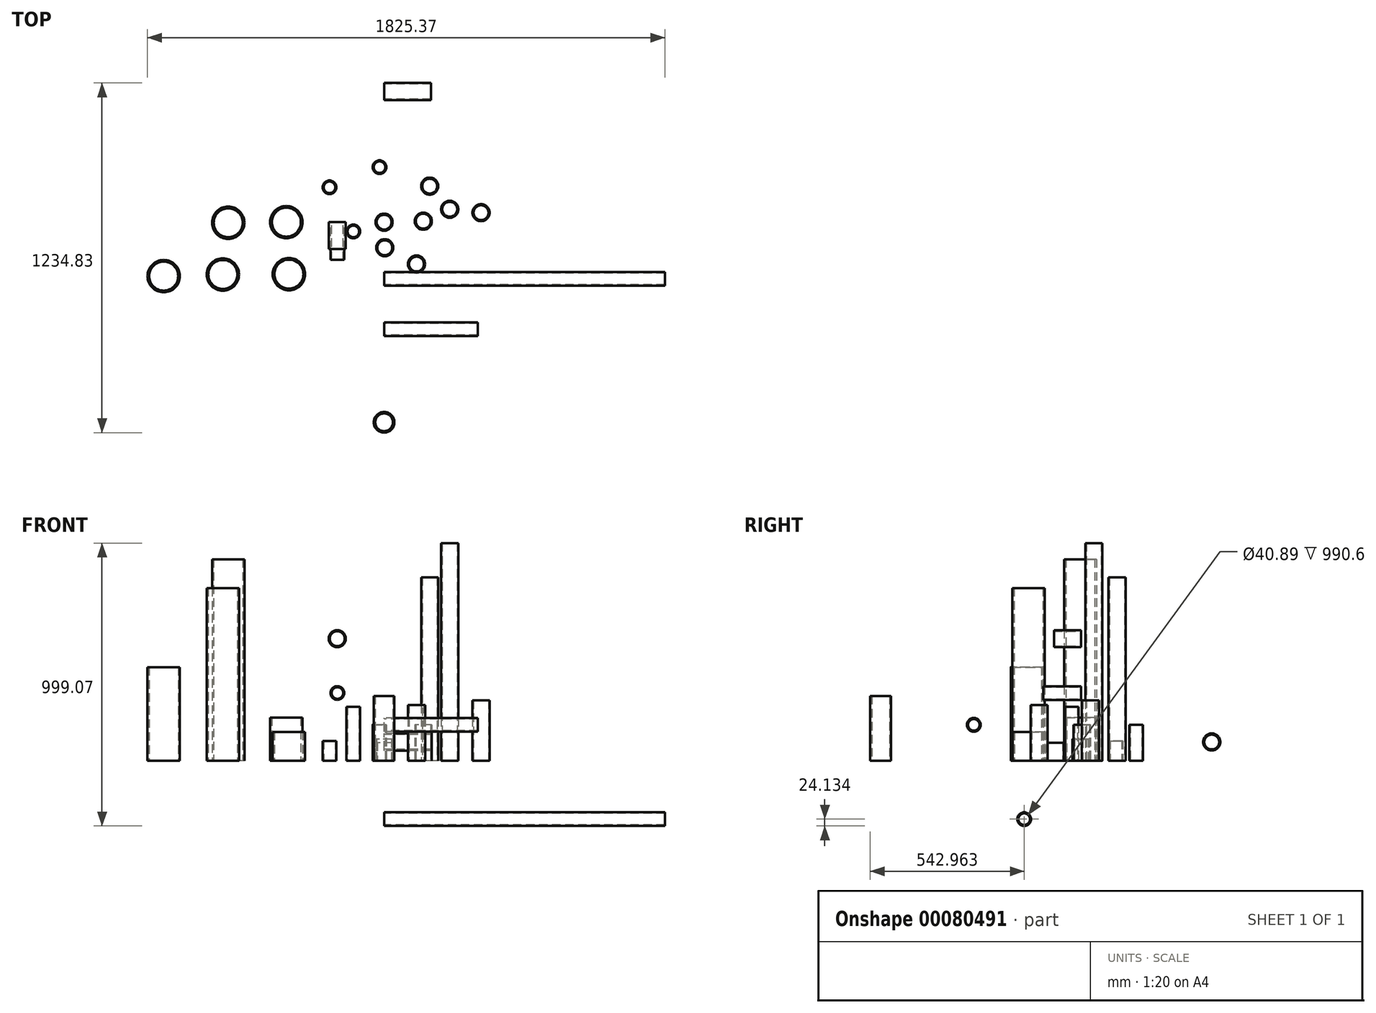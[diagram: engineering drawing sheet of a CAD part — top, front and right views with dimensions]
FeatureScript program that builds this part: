
annotation { "Feature Type Name" : "Feature", "Feature Type Description" : "" }
export const myFeature = defineFeature(function(context is Context, id is Id, definition is map)
    precondition{}
    {
        {
            var Q0;
            Q0=qCreatedBy(makeId("Top.planeOp"),FACE);
            var sketch = newSketch(context, id + "F0", { "sketchPlane" : qUnion([Q0])});
            skCircle(sketch, "E0", {"center": v(0, 0) * mm, "radius": 30.16 * mm});
            skCircle(sketch, "E1", {"center": v(0, 0) * mm, "radius": 26.25 * mm});
            skSolve(sketch);
        }
        {
            var Q0;
            Q0=makeQuery(id+"F0.imprint","IMPRINT",FACE,{"disambiguationData":[TD([[makeQuery(id+"F0.imprint","IMPRINT",EDGE,{"derivedFrom":sQuery(id+"F0.wireOp",EDGE,"E0")}),1.0]])]});
            extrude(context, id + "F1", {"entities" : qUnion([Q0]), "depth" : 76.2 * mm});
        }
        {
            var Q0;
            Q0=qCreatedBy(makeId("Top.planeOp"),FACE);
            var sketch = newSketch(context, id + "F2", { "sketchPlane" : qUnion([Q0])});
            skCircle(sketch, "E2", {"center": v(138.3, 3.34) * mm, "radius": 30.16 * mm});
            skCircle(sketch, "E3", {"center": v(138.3, 3.34) * mm, "radius": 26.25 * mm});
            skSolve(sketch);
        }
        {
            var Q0;
            Q0=makeQuery(id+"F2.imprint","IMPRINT",FACE,{"disambiguationData":[TD([[makeQuery(id+"F2.imprint","IMPRINT",EDGE,{"derivedFrom":sQuery(id+"F2.wireOp",EDGE,"E2")}),1.0]])]});
            extrude(context, id + "F3", {"entities" : qUnion([Q0]), "depth" : 127 * mm});
        }
        {
            var Q0;
            Q0=qCreatedBy(makeId("Top.planeOp"),FACE);
            var sketch = newSketch(context, id + "F4", { "sketchPlane" : qUnion([Q0])});
            skCircle(sketch, "E4", {"center": v(231.52, 45.5) * mm, "radius": 30.16 * mm});
            skCircle(sketch, "E5", {"center": v(231.52, 45.5) * mm, "radius": 26.25 * mm});
            skSolve(sketch);
        }
        {
            var Q0;
            Q0=makeQuery(id+"F4.imprint","IMPRINT",FACE,{"disambiguationData":[TD([[makeQuery(id+"F4.imprint","IMPRINT",EDGE,{"derivedFrom":sQuery(id+"F4.wireOp",EDGE,"E4")}),1.0]])]});
            extrude(context, id + "F5", {"entities" : qUnion([Q0]), "depth" : 768.35 * mm});
        }
        {
            var Q0;
            Q0=qCreatedBy(makeId("Right.planeOp"),FACE);
            var sketch = newSketch(context, id + "F6", { "sketchPlane" : qUnion([Q0])});
            skCircle(sketch, "E6", {"center": v(461.28, 65.95) * mm, "radius": 30.16 * mm});
            skCircle(sketch, "E7", {"center": v(461.28, 65.95) * mm, "radius": 26.25 * mm});
            skSolve(sketch);
        }
        {
            var Q0;
            Q0=makeQuery(id+"F6.imprint","IMPRINT",FACE,{"disambiguationData":[TD([[makeQuery(id+"F6.imprint","IMPRINT",EDGE,{"derivedFrom":sQuery(id+"F6.wireOp",EDGE,"E6")}),1.0]])]});
            extrude(context, id + "F7", {"entities" : qUnion([Q0]), "depth" : 165.1 * mm});
        }
        {
            var Q0;
            Q0=qCreatedBy(makeId("Top.planeOp"),FACE);
            var sketch = newSketch(context, id + "F8", { "sketchPlane" : qUnion([Q0])});
            skCircle(sketch, "E8", {"center": v(-192.6, 123.01) * mm, "radius": 24.13 * mm});
            skCircle(sketch, "E9", {"center": v(-192.6, 123.01) * mm, "radius": 20.45 * mm});
            skSolve(sketch);
        }
        {
            var Q0;
            Q0=qCreatedBy(makeId("Front.planeOp"),FACE);
            var sketch = newSketch(context, id + "F9", { "sketchPlane" : qUnion([Q0])});
            skCircle(sketch, "E10", {"center": v(-164.87, 238.92) * mm, "radius": 24.13 * mm});
            skCircle(sketch, "E11", {"center": v(-164.87, 238.92) * mm, "radius": 20.45 * mm});
            skSolve(sketch);
        }
        {
            var Q0;
            Q0 = qSketchRegion(id + "F9", true);
            extrude(context, id + "F10", {"entities" : qUnion([Q0]), "depth" : 133.35 * mm});
        }
        {
            var Q0;
            Q0=qCreatedBy(makeId("Right.planeOp"),FACE);
            var sketch = newSketch(context, id + "F11", { "sketchPlane" : qUnion([Q0])});
            skCircle(sketch, "E12", {"center": v(-378.27, 126.43) * mm, "radius": 20.45 * mm});
            skCircle(sketch, "E13", {"center": v(-378.27, 126.43) * mm, "radius": 24.13 * mm});
            skSolve(sketch);
        }
        {
            var Q0;
            Q0 = qSketchRegion(id + "F11", true);
            extrude(context, id + "F12", {"entities" : qUnion([Q0]), "depth" : 330.2 * mm});
        }
        {
            var Q0;
            Q0=qCreatedBy(makeId("Top.planeOp"),FACE);
            var sketch = newSketch(context, id + "F13", { "sketchPlane" : qUnion([Q0])});
            skCircle(sketch, "E14", {"center": v(-16.24, 194.12) * mm, "radius": 24.13 * mm});
            skCircle(sketch, "E15", {"center": v(-16.24, 194.12) * mm, "radius": 20.45 * mm});
            skSolve(sketch);
        }
        {
            var Q0;
            Q0 = qSketchRegion(id + "F13", true);
            extrude(context, id + "F14", {"entities" : qUnion([Q0]), "depth" : 127 * mm});
        }
        {
            var Q0;
            Q0=qCreatedBy(makeId("Right.planeOp"),FACE);
            var sketch = newSketch(context, id + "F15", { "sketchPlane" : qUnion([Q0])});
            skCircle(sketch, "E16", {"center": v(-200.43, -206.59) * mm, "radius": 24.13 * mm});
            skCircle(sketch, "E17", {"center": v(-200.43, -206.59) * mm, "radius": 20.45 * mm});
            skSolve(sketch);
        }
        {
            var Q0;
            Q0 = qSketchRegion(id + "F15", true);
            extrude(context, id + "F16", {"entities" : qUnion([Q0]), "depth" : 990.6 * mm});
        }
        {
            var Q0;
            Q0=makeQuery(id+"F8.imprint","IMPRINT",FACE,{"disambiguationData":[TD([[makeQuery(id+"F8.imprint","IMPRINT",EDGE,{"derivedFrom":sQuery(id+"F8.wireOp",EDGE,"E8")}),1.0]])]});
            extrude(context, id + "F17", {"entities" : qUnion([Q0]), "depth" : 69.85 * mm});
        }
        {
            var Q0;
            Q0=qCreatedBy(makeId("Top.planeOp"),FACE);
            var sketch = newSketch(context, id + "F18", { "sketchPlane" : qUnion([Q0])});
            skCircle(sketch, "E18", {"center": v(-108.42, -32.85) * mm, "radius": 24.13 * mm});
            skCircle(sketch, "E19", {"center": v(-108.42, -32.85) * mm, "radius": 20.45 * mm});
            skSolve(sketch);
        }
        {
            var Q0;
            Q0=makeQuery(id+"F18.imprint","IMPRINT",FACE,{"disambiguationData":[TD([[makeQuery(id+"F18.imprint","IMPRINT",EDGE,{"derivedFrom":sQuery(id+"F18.wireOp",EDGE,"E18")}),1.0]])]});
            extrude(context, id + "F19", {"entities" : qUnion([Q0]), "depth" : 190.5 * mm});
        }
        {
            var Q0;
            Q0=qCreatedBy(makeId("Top.planeOp"),FACE);
            var sketch = newSketch(context, id + "F20", { "sketchPlane" : qUnion([Q0])});
            skCircle(sketch, "E20", {"center": v(160.85, 127.18) * mm, "radius": 30.16 * mm});
            skCircle(sketch, "E21", {"center": v(160.85, 127.18) * mm, "radius": 26.25 * mm});
            skSolve(sketch);
        }
        {
            var Q0;
            Q0=makeQuery(id+"F20.imprint","IMPRINT",FACE,{"disambiguationData":[TD([[makeQuery(id+"F20.imprint","IMPRINT",EDGE,{"derivedFrom":sQuery(id+"F20.wireOp",EDGE,"E20")}),1.0]])]});
            extrude(context, id + "F21", {"entities" : qUnion([Q0]), "depth" : 647.7 * mm});
        }
        {
            var Q0;
            Q0=qCreatedBy(makeId("Top.planeOp"),FACE);
            var sketch = newSketch(context, id + "F22", { "sketchPlane" : qUnion([Q0])});
            skCircle(sketch, "E22", {"center": v(-345, 0) * mm, "radius": 57.15 * mm});
            skCircle(sketch, "E23", {"center": v(-345, 0) * mm, "radius": 51.13 * mm});
            skSolve(sketch);
        }
        {
            var Q0;
            Q0=makeQuery(id+"F22.imprint","IMPRINT",FACE,{"disambiguationData":[TD([[makeQuery(id+"F22.imprint","IMPRINT",EDGE,{"derivedFrom":sQuery(id+"F22.wireOp",EDGE,"E22")}),1.0]])]});
            extrude(context, id + "F23", {"entities" : qUnion([Q0]), "depth" : 152.4 * mm});
        }
        {
            var Q0;
            Q0=qCreatedBy(makeId("Top.planeOp"),FACE);
            var sketch = newSketch(context, id + "F24", { "sketchPlane" : qUnion([Q0])});
            skCircle(sketch, "E24", {"center": v(-549.98, -2.17) * mm, "radius": 57.15 * mm});
            skCircle(sketch, "E25", {"center": v(-549.98, -2.17) * mm, "radius": 51.13 * mm});
            skSolve(sketch);
        }
        {
            var Q0;
            Q0=makeQuery(id+"F24.imprint","IMPRINT",FACE,{"disambiguationData":[TD([[makeQuery(id+"F24.imprint","IMPRINT",EDGE,{"derivedFrom":sQuery(id+"F24.wireOp",EDGE,"E24")}),1.0]])]});
            extrude(context, id + "F25", {"entities" : qUnion([Q0]), "depth" : 711.2 * mm});
        }
        {
            var Q0;
            Q0=qCreatedBy(makeId("Top.planeOp"),FACE);
            var sketch = newSketch(context, id + "F26", { "sketchPlane" : qUnion([Q0])});
            skCircle(sketch, "E26", {"center": v(-335.9, -183.7) * mm, "radius": 57.15 * mm});
            skCircle(sketch, "E27", {"center": v(-335.9, -183.7) * mm, "radius": 51.13 * mm});
            skSolve(sketch);
        }
        {
            var Q0;
            Q0=makeQuery(id+"F26.imprint","IMPRINT",FACE,{"disambiguationData":[TD([[makeQuery(id+"F26.imprint","IMPRINT",EDGE,{"derivedFrom":sQuery(id+"F26.wireOp",EDGE,"E26")}),1.0]])]});
            extrude(context, id + "F27", {"entities" : qUnion([Q0]), "depth" : 101.6 * mm});
        }
        {
            var Q0;
            Q0=qCreatedBy(makeId("Top.planeOp"),FACE);
            var sketch = newSketch(context, id + "F28", { "sketchPlane" : qUnion([Q0])});
            skCircle(sketch, "E28", {"center": v(-568.97, -184.87) * mm, "radius": 57.15 * mm});
            skCircle(sketch, "E29", {"center": v(-568.97, -184.87) * mm, "radius": 51.13 * mm});
            skSolve(sketch);
        }
        {
            var Q0;
            Q0=makeQuery(id+"F28.imprint","IMPRINT",FACE,{"disambiguationData":[TD([[makeQuery(id+"F28.imprint","IMPRINT",EDGE,{"derivedFrom":sQuery(id+"F28.wireOp",EDGE,"E28")}),1.0]])]});
            extrude(context, id + "F29", {"entities" : qUnion([Q0]), "depth" : 609.6 * mm});
        }
        {
            var Q0;
            Q0=qCreatedBy(makeId("Top.planeOp"),FACE);
            var sketch = newSketch(context, id + "F30", { "sketchPlane" : qUnion([Q0])});
            skCircle(sketch, "E30", {"center": v(-777.62, -190.68) * mm, "radius": 57.15 * mm});
            skCircle(sketch, "E31", {"center": v(-777.62, -190.68) * mm, "radius": 51.13 * mm});
            skSolve(sketch);
        }
        {
            var Q0;
            Q0=makeQuery(id+"F30.imprint","IMPRINT",FACE,{"disambiguationData":[TD([[makeQuery(id+"F30.imprint","IMPRINT",EDGE,{"derivedFrom":sQuery(id+"F30.wireOp",EDGE,"E30")}),1.0]])]});
            extrude(context, id + "F31", {"entities" : qUnion([Q0]), "depth" : 330.2 * mm});
        }
        {
            var Q0;
            Q0=qCreatedBy(makeId("Top.planeOp"),FACE);
            var sketch = newSketch(context, id + "F32", { "sketchPlane" : qUnion([Q0])});
            skCircle(sketch, "E32", {"center": v(342.1, 33.53) * mm, "radius": 30.16 * mm});
            skCircle(sketch, "E33", {"center": v(342.1, 33.53) * mm, "radius": 26.25 * mm});
            skSolve(sketch);
        }
        {
            var Q0;
            Q0=makeQuery(id+"F32.imprint","IMPRINT",FACE,{"disambiguationData":[TD([[makeQuery(id+"F32.imprint","IMPRINT",EDGE,{"derivedFrom":sQuery(id+"F32.wireOp",EDGE,"E32")}),1.0]])]});
            extrude(context, id + "F33", {"entities" : qUnion([Q0]), "depth" : 212.72 * mm});
        }
        {
            var Q0;
            Q0=qCreatedBy(makeId("Front.planeOp"),FACE);
            var sketch = newSketch(context, id + "F34", { "sketchPlane" : qUnion([Q0])});
            skCircle(sketch, "E34", {"center": v(-165.35, 430.8) * mm, "radius": 30.16 * mm});
            skCircle(sketch, "E35", {"center": v(-165.35, 430.8) * mm, "radius": 26.25 * mm});
            skSolve(sketch);
        }
        {
            var Q0;
            Q0=makeQuery(id+"F34.imprint","IMPRINT",FACE,{"disambiguationData":[TD([[makeQuery(id+"F34.imprint","IMPRINT",EDGE,{"derivedFrom":sQuery(id+"F34.wireOp",EDGE,"E34")}),1.0]])]});
            extrude(context, id + "F35", {"entities" : qUnion([Q0]), "depth" : 95.25 * mm});
        }
        {
            var Q0;
            Q0=qCreatedBy(makeId("Top.planeOp"),FACE);
            var sketch = newSketch(context, id + "F36", { "sketchPlane" : qUnion([Q0])});
            skCircle(sketch, "E36", {"center": v(2.35, -90.32) * mm, "radius": 30.16 * mm});
            skCircle(sketch, "E37", {"center": v(2.35, -90.32) * mm, "radius": 26.25 * mm});
            skSolve(sketch);
        }
        {
            var Q0;
            Q0=makeQuery(id+"F36.imprint","IMPRINT",FACE,{"disambiguationData":[TD([[makeQuery(id+"F36.imprint","IMPRINT",EDGE,{"derivedFrom":sQuery(id+"F36.wireOp",EDGE,"E36")}),1.0]])]});
            extrude(context, id + "F37", {"entities" : qUnion([Q0]), "depth" : 63.5 * mm});
        }
        {
            var Q0;
            Q0=qCreatedBy(makeId("Top.planeOp"),FACE);
            var sketch = newSketch(context, id + "F38", { "sketchPlane" : qUnion([Q0])});
            skCircle(sketch, "E38", {"center": v(114.34, -147.96) * mm, "radius": 30.16 * mm});
            skCircle(sketch, "E39", {"center": v(114.34, -147.96) * mm, "radius": 26.25 * mm});
            skSolve(sketch);
        }
        {
            var Q0;
            Q0=makeQuery(id+"F38.imprint","IMPRINT",FACE,{"disambiguationData":[TD([[makeQuery(id+"F38.imprint","IMPRINT",EDGE,{"derivedFrom":sQuery(id+"F38.wireOp",EDGE,"E38")}),1.0]])]});
            extrude(context, id + "F39", {"entities" : qUnion([Q0]), "depth" : 196.85 * mm});
        }
        {
            var Q0;
            Q0=qCreatedBy(makeId("Top.planeOp"),FACE);
            var sketch = newSketch(context, id + "F40", { "sketchPlane" : qUnion([Q0])});
            skCircle(sketch, "E40", {"center": v(0, -706.88) * mm, "radius": 31.36 * mm});
            skCircle(sketch, "E41", {"center": v(0, -706.88) * mm, "radius": 36.51 * mm});
            skSolve(sketch);
        }
        {
            var Q0;
            Q0=makeQuery(id+"F40.imprint","IMPRINT",FACE,{"disambiguationData":[TD([[makeQuery(id+"F40.imprint","IMPRINT",EDGE,{"derivedFrom":sQuery(id+"F40.wireOp",EDGE,"E40")}),-1.0]])]});
            extrude(context, id + "F41", {"entities" : qUnion([Q0]), "depth" : 228.6 * mm});
        }
    });
